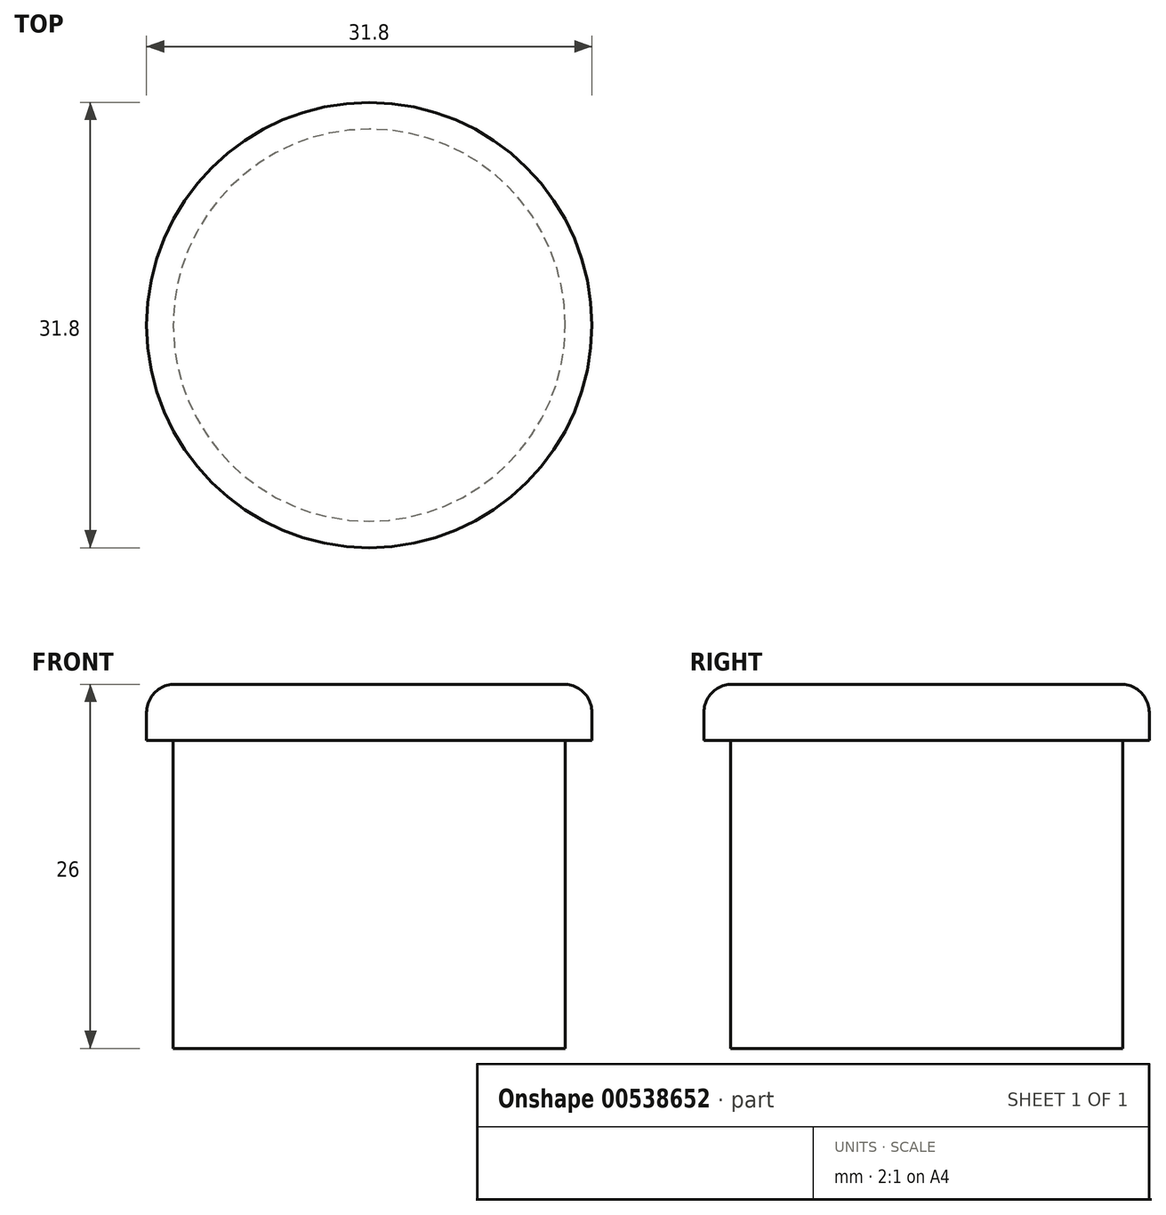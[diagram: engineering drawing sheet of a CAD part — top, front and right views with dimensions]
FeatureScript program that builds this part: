
annotation { "Feature Type Name" : "Feature", "Feature Type Description" : "" }
export const myFeature = defineFeature(function(context is Context, id is Id, definition is map)
    precondition{}
    {
        {
            var Q0;
            Q0=qCreatedBy(makeId("Front.planeOp"),FACE);
            var sketch = newSketch(context, id + "F0", { "sketchPlane" : qUnion([Q0])});
            skLineSegment(sketch, "E0", {"start": v(0, 26) * mm, "end": v(15.9, 26) * mm});
            skLineSegment(sketch, "E1", {"start": v(15.9, 26) * mm, "end": v(15.9, 22) * mm});
            skLineSegment(sketch, "E2", {"start": v(15.9, 22) * mm, "end": v(14, 22) * mm});
            skLineSegment(sketch, "E3", {"start": v(14, 22) * mm, "end": v(14, 0) * mm});
            skLineSegment(sketch, "E4", {"start": v(14, 0) * mm, "end": v(0, 0) * mm});
            skLineSegment(sketch, "E5", {"start": v(0, 0) * mm, "end": v(0, 26) * mm});
            skSolve(sketch);
        }
        {
            var Q0;
            Q0=qCreatedBy(makeId("Front.planeOp"),FACE);
            var sketch = newSketch(context, id + "F1", { "sketchPlane" : qUnion([Q0])});
            skLineSegment(sketch, "E6", {"start": v(0, 36.07) * mm, "end": v(0, -14.81) * mm, "construction": true});
            skSolve(sketch);
        }
        {
            var Q0;
            Q0=makeQuery(id+"F0.imprint","IMPRINT",FACE,{"disambiguationData":[TD([[makeQuery(id+"F0.imprint","IMPRINT",EDGE,{"derivedFrom":sQuery(id+"F0.wireOp",EDGE,"E0")}),-1.0]])]});
            var Q1;
            Q1=sQuery(id+"F1.wireOp",EDGE,"E6");
            revolve(context, id + "F2", {"entities" : qUnion([Q0]), "axis" : qUnion([Q1]), "revolveType" : RevolveType.FULL});
        }
        {
            var Q0;
            Q0=makeQuery(id+"F2.opRevolve","SWEPT_EDGE",EDGE,{"disambiguationData":[OSD([sQuery(id+"F0.wireOp",EDGE,"E0"),sQuery(id+"F0.wireOp",EDGE,"E1")])]});
            fillet(context, id + "F3", {"entities" : qUnion([Q0]), "radius" : 2 * mm, "tangentPropagation" : true, "allowEdgeOverflow" : false});
        }
    });
